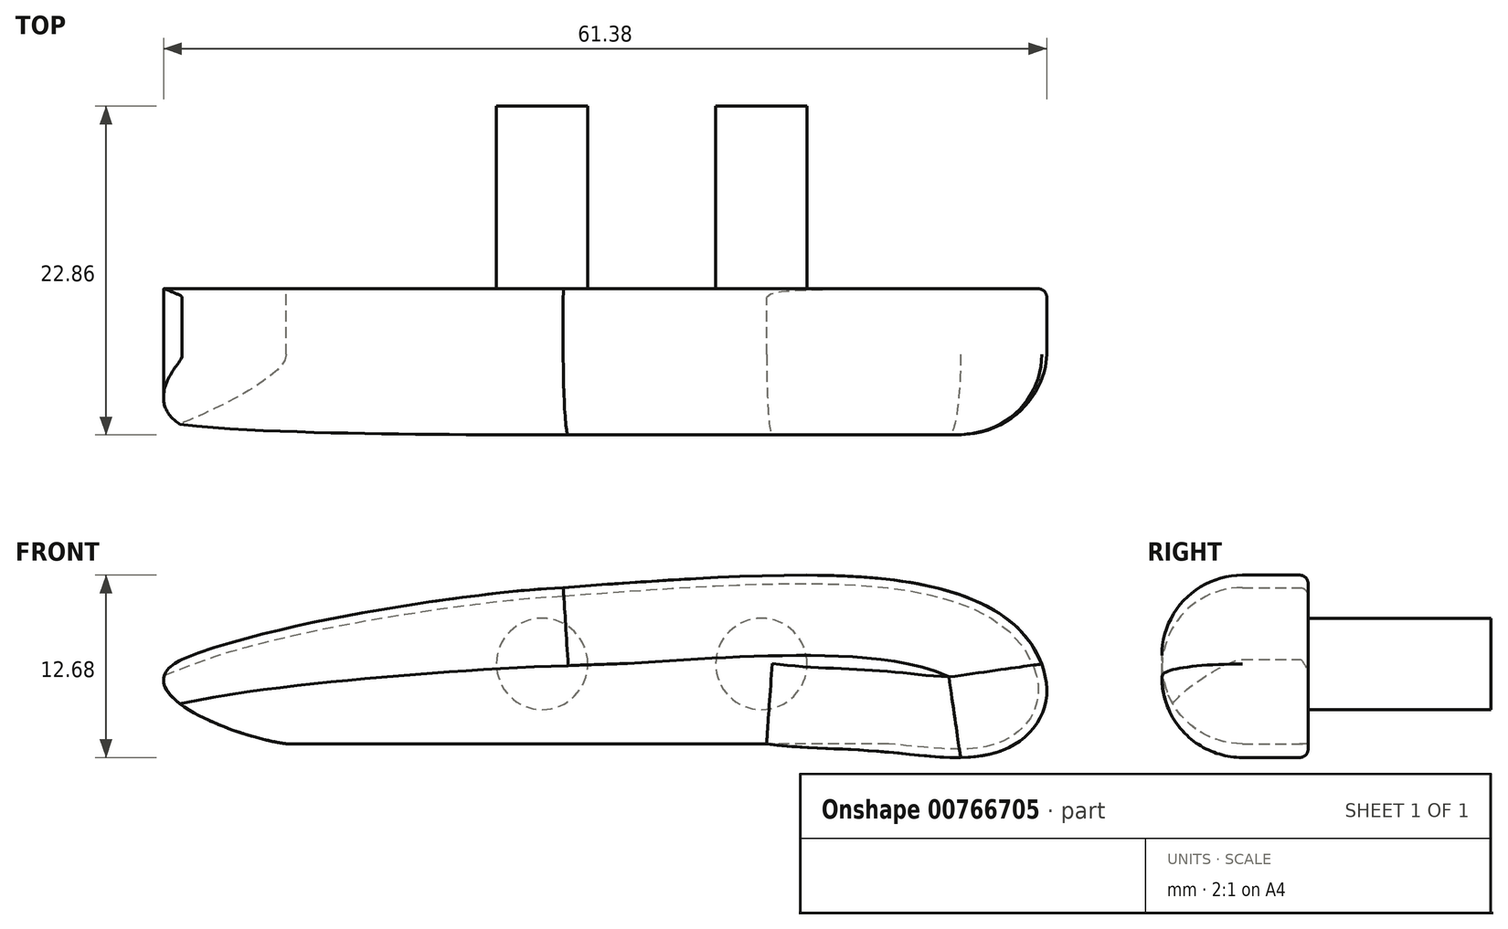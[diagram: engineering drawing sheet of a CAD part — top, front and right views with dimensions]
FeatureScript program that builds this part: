
annotation { "Feature Type Name" : "Feature", "Feature Type Description" : "" }
export const myFeature = defineFeature(function(context is Context, id is Id, definition is map)
    precondition{}
    {
        {
            var Q0;
            Q0=qCreatedBy(makeId("Front.planeOp"),FACE);
            var sketch = newSketch(context, id + "F0", { "sketchPlane" : qUnion([Q0])});
            skCircle(sketch, "E0", {"center": v(9.34, 19.4) * mm, "radius": 3.18 * mm});
            skCircle(sketch, "E1", {"center": v(-5.9, 19.4) * mm, "radius": 3.18 * mm});
            skLineSegment(sketch, "E2", {"start": v(-5.9, 13.84) * mm, "end": v(9.7, 13.84) * mm});
            skLineSegment(sketch, "E3", {"start": v(-5.9, 13.84) * mm, "end": v(-23.68, 13.84) * mm});
            skFitSpline(sketch, "E4", {"points": [v(-23.68, 13.84) * mm, v(-30.92, 19.72) * mm], "startDerivative": vector(-11.67, 1.56) * mm, "endDerivative": vector(13.07, 6.38) * mm});
            skFitSpline(sketch, "E5", {"points": [v(-30.92, 19.72) * mm, v(-4.43, 24.7) * mm], "startDerivative": vector(20.37, 8.2) * mm, "endDerivative": vector(17.93, 0.91) * mm});
            skFitSpline(sketch, "E6", {"points": [v(-4.43, 24.7) * mm, v(21.42, 24.7) * mm, v(27.75, 21.26) * mm, v(29.05, 16.56) * mm, v(25.83, 13.28) * mm, v(19.17, 13.16) * mm, v(14.52, 13.5) * mm, v(9.7, 13.84) * mm], "startDerivative": vector(150.1, 11.51) * mm, "endDerivative": vector(-44, 6.2) * mm});
            skLineSegment(sketch, "E7", {"start": v(9.34, 19.4) * mm, "end": v(33.23, 19.4) * mm});
            skSolve(sketch);
        }
        {
            var Q0;
            Q0=makeQuery(id+"F0.imprint","IMPRINT",FACE,{"disambiguationData":[TD([[makeQuery(id+"F0.imprint","IMPRINT",EDGE,{"derivedFrom":sQuery(id+"F0.wireOp",EDGE,"E0")}),-1.0]])]});
            var Q1;
            Q1=makeQuery(id+"F0.imprint","IMPRINT",FACE,{"disambiguationData":[TD([[makeQuery(id+"F0.imprint","IMPRINT",EDGE,{"derivedFrom":sQuery(id+"F0.wireOp",EDGE,"E1")}),1.0]])]});
            var Q2;
            Q2=makeQuery(id+"F0.imprint","IMPRINT",FACE,{"disambiguationData":[TD([[makeQuery(id+"F0.imprint","IMPRINT",EDGE,{"derivedFrom":sQuery(id+"F0.wireOp",EDGE,"E0")}),1.0]])]});
            extrude(context, id + "F1", {"entities" : qUnion([Q0, Q1, Q2]), "depth" : 10.16 * mm, "offsetDistance" : 25.4 * mm});
        }
        {
            var Q0;
            Q0=makeQuery(id+"F1.opExtrude","CAP_EDGE",EDGE,{"disambiguationData":[OSD([sQuery(id+"F0.wireOp",EDGE,"E6")])],"isStart":false});
            var Q1;
            Q1=makeQuery(id+"F1.opExtrude","CAP_EDGE",EDGE,{"disambiguationData":[OSD([sQuery(id+"F0.wireOp",EDGE,"E5")])],"isStart":false});
            var Q2;
            Q2=makeQuery(id+"F1.opExtrude","CAP_EDGE",EDGE,{"disambiguationData":[OSD([sQuery(id+"F0.wireOp",EDGE,"E2"),sQuery(id+"F0.wireOp",EDGE,"E3")])],"isStart":false});
            fillet(context, id + "F2", {"entities" : qUnion([Q0, Q1, Q2]), "radius" : 5.6 * mm, "tangentPropagation" : true, "allowEdgeOverflow" : false});
        }
        {
            var Q0;
            Q0=makeQuery(id+"F0.imprint","IMPRINT",FACE,{"disambiguationData":[TD([[makeQuery(id+"F0.imprint","IMPRINT",EDGE,{"derivedFrom":sQuery(id+"F0.wireOp",EDGE,"E0")}),1.0]])]});
            var Q1;
            Q1=makeQuery(id+"F0.imprint","IMPRINT",FACE,{"disambiguationData":[TD([[makeQuery(id+"F0.imprint","IMPRINT",EDGE,{"derivedFrom":sQuery(id+"F0.wireOp",EDGE,"E1")}),1.0]])]});
            extrude(context, id + "F3", {"entities" : qUnion([Q0, Q1]), "operationType" : NewBodyOperationType.ADD, "depth" : -12.7 * mm, "offsetDistance" : 25.4 * mm});
        }
        {
            var Q0;
            Q0=makeQuery(id+"F1.opExtrude","CAP_EDGE",EDGE,{"disambiguationData":[OSD([sQuery(id+"F0.wireOp",EDGE,"E6")])],"isStart":true});
            fillet(context, id + "F4", {"entities" : qUnion([Q0]), "radius" : 0.58 * mm, "tangentPropagation" : true, "allowEdgeOverflow" : false});
        }
    });
